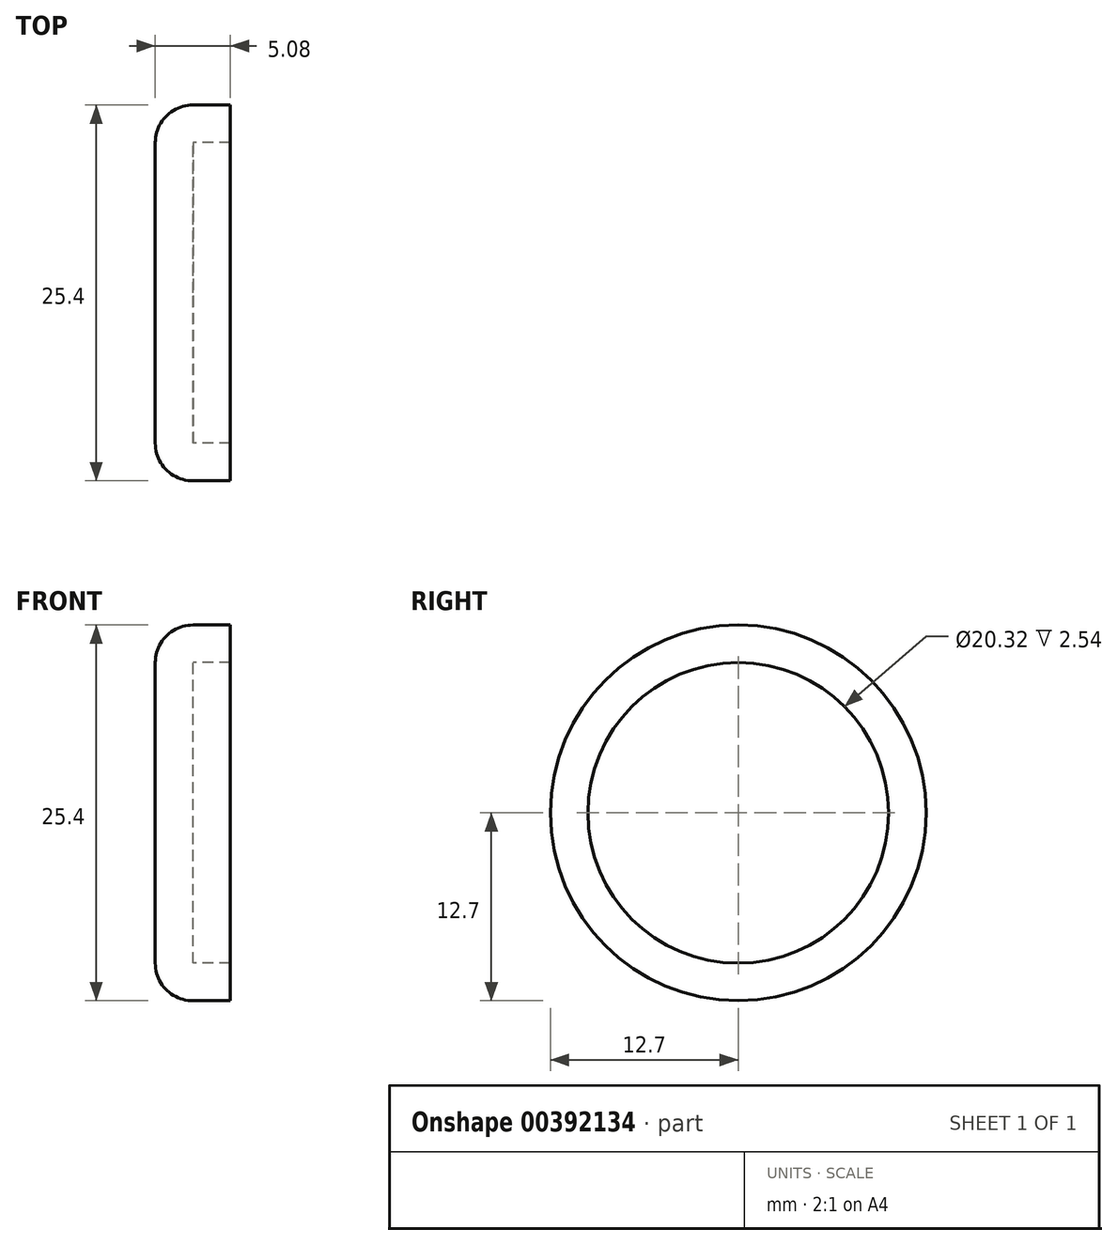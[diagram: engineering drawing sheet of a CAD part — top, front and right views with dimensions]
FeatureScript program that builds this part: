
annotation { "Feature Type Name" : "Feature", "Feature Type Description" : "" }
export const myFeature = defineFeature(function(context is Context, id is Id, definition is map)
    precondition{}
    {
        {
            var Q0;
            Q0=qCreatedBy(makeId("Right.planeOp"),FACE);
            var sketch = newSketch(context, id + "F0", { "sketchPlane" : qUnion([Q0])});
            skCircle(sketch, "E0", {"center": v(0, 0) * mm, "radius": 12.7 * mm});
            skSolve(sketch);
        }
        {
            var Q0;
            Q0=makeQuery(id+"F0.imprint","IMPRINT",FACE,{"disambiguationData":[TD([[makeQuery(id+"F0.imprint","IMPRINT",EDGE,{"derivedFrom":sQuery(id+"F0.wireOp",EDGE,"E0")}),1.0]])]});
            extrude(context, id + "F1", {"entities" : qUnion([Q0]), "depth" : 5.08 * mm});
        }
        {
            var Q0;
            Q0=makeQuery(id+"F1.opExtrude","CAP_EDGE",EDGE,{"disambiguationData":[OSD([sQuery(id+"F0.wireOp",EDGE,"E0")])],"isStart":true});
            fillet(context, id + "F2", {"entities" : qUnion([Q0]), "radius" : 2.54 * mm, "tangentPropagation" : true, "allowEdgeOverflow" : false});
        }
        {
            var Q0;
            Q0=makeQuery(id+"F1.opExtrude","CAP_FACE",FACE,{"disambiguationData":[OSD([sQuery(id+"F0.wireOp",EDGE,"E0")])],"isStart":false});
            var Q1;
            Q1=makeQuery(id+"F1.opExtrude","SWEPT_BODY",BODY,{"disambiguationData":[OSD([sQuery(id+"F0.wireOp",EDGE,"E0")])]});
            shell(context, id + "F3", {"entities" : qUnion([Q0]), "parts" : qUnion([Q1]), "thickness" : 2.54 * mm});
        }
    });
